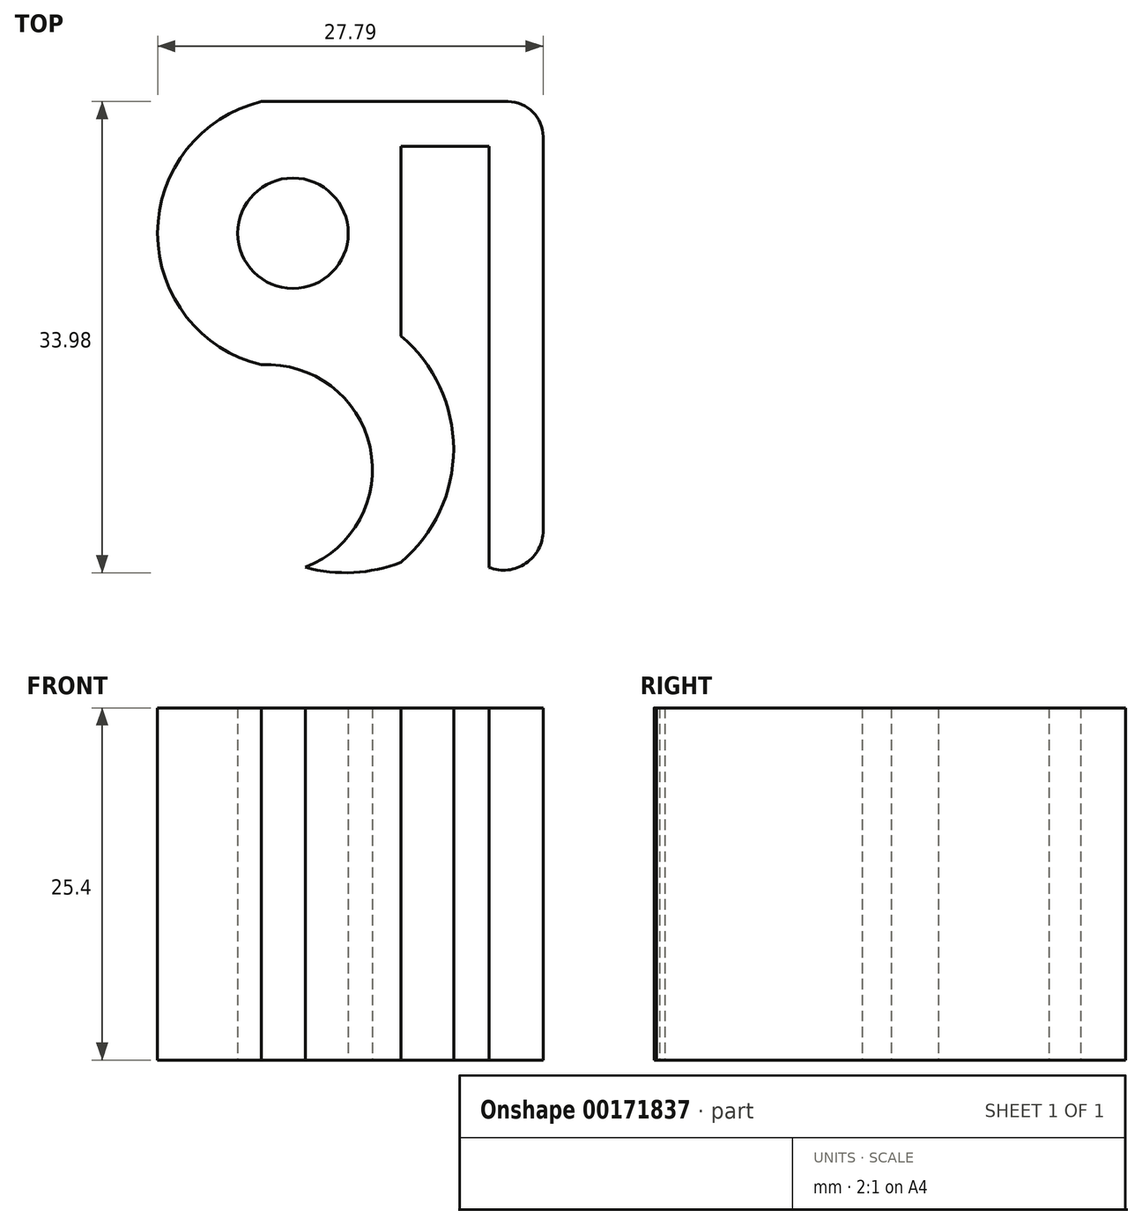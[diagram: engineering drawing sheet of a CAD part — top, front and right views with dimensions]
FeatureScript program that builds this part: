
annotation { "Feature Type Name" : "Feature", "Feature Type Description" : "" }
export const myFeature = defineFeature(function(context is Context, id is Id, definition is map)
    precondition{}
    {
        {
            var Q0;
            Q0=qCreatedBy(makeId("Top.planeOp"),FACE);
            var sketch = newSketch(context, id + "F0", { "sketchPlane" : qUnion([Q0])});
            skLineSegment(sketch, "E0", {"start": v(-10.25, 24.77) * mm, "end": v(-10.25, 38.44) * mm});
            skLineSegment(sketch, "E1", {"start": v(-10.25, 38.44) * mm, "end": v(-3.9, 38.44) * mm});
            skLineSegment(sketch, "E2", {"start": v(-3.9, 38.44) * mm, "end": v(-3.9, 8.07) * mm});
            skLineSegment(sketch, "E3", {"start": v(-20.31, 41.67) * mm, "end": v(-2.54, 41.67) * mm});
            skLineSegment(sketch, "E4", {"start": v(0, 39.13) * mm, "end": v(0, 10.72) * mm});
            skArc(sketch, "E5", {"start": v(-10.25, 8.45) * mm, "mid": v(-6.45, 16.6) * mm, "end": v(-10.25, 24.77) * mm});
            skArc(sketch, "E6", {"start": v(-17.13, 8.08) * mm, "mid": v(-12.48, 16.74) * mm, "end": v(-20.31, 22.68) * mm});
            skArc(sketch, "E7", {"start": v(-17.13, 8.08) * mm, "mid": v(-13.66, 7.7) * mm, "end": v(-10.25, 8.45) * mm});
            skCircle(sketch, "E8", {"center": v(-18.03, 32.17) * mm, "radius": 3.98 * mm});
            skArc(sketch, "E9", {"start": v(-20.31, 41.67) * mm, "mid": v(-27.8, 32.17) * mm, "end": v(-20.31, 22.68) * mm});
            skArc(sketch, "E10", {"start": v(0, 10.72) * mm, "mid": v(-1.25, 8.37) * mm, "end": v(-3.9, 8.07) * mm});
            skPoint(sketch, "E11.visualSharp", {"position": v(0, 41.67) * mm});
            skArc(sketch, "E11.filletArc", {"start": v(0, 39.13) * mm, "mid": v(-0.74, 40.92) * mm, "end": v(-2.54, 41.67) * mm});
            skSolve(sketch);
        }
        {
            var Q0;
            Q0 = qSketchRegion(id + "F0", true);
            extrude(context, id + "F1", {"entities" : qUnion([Q0]), "depth" : 25.4 * mm});
        }
    });
